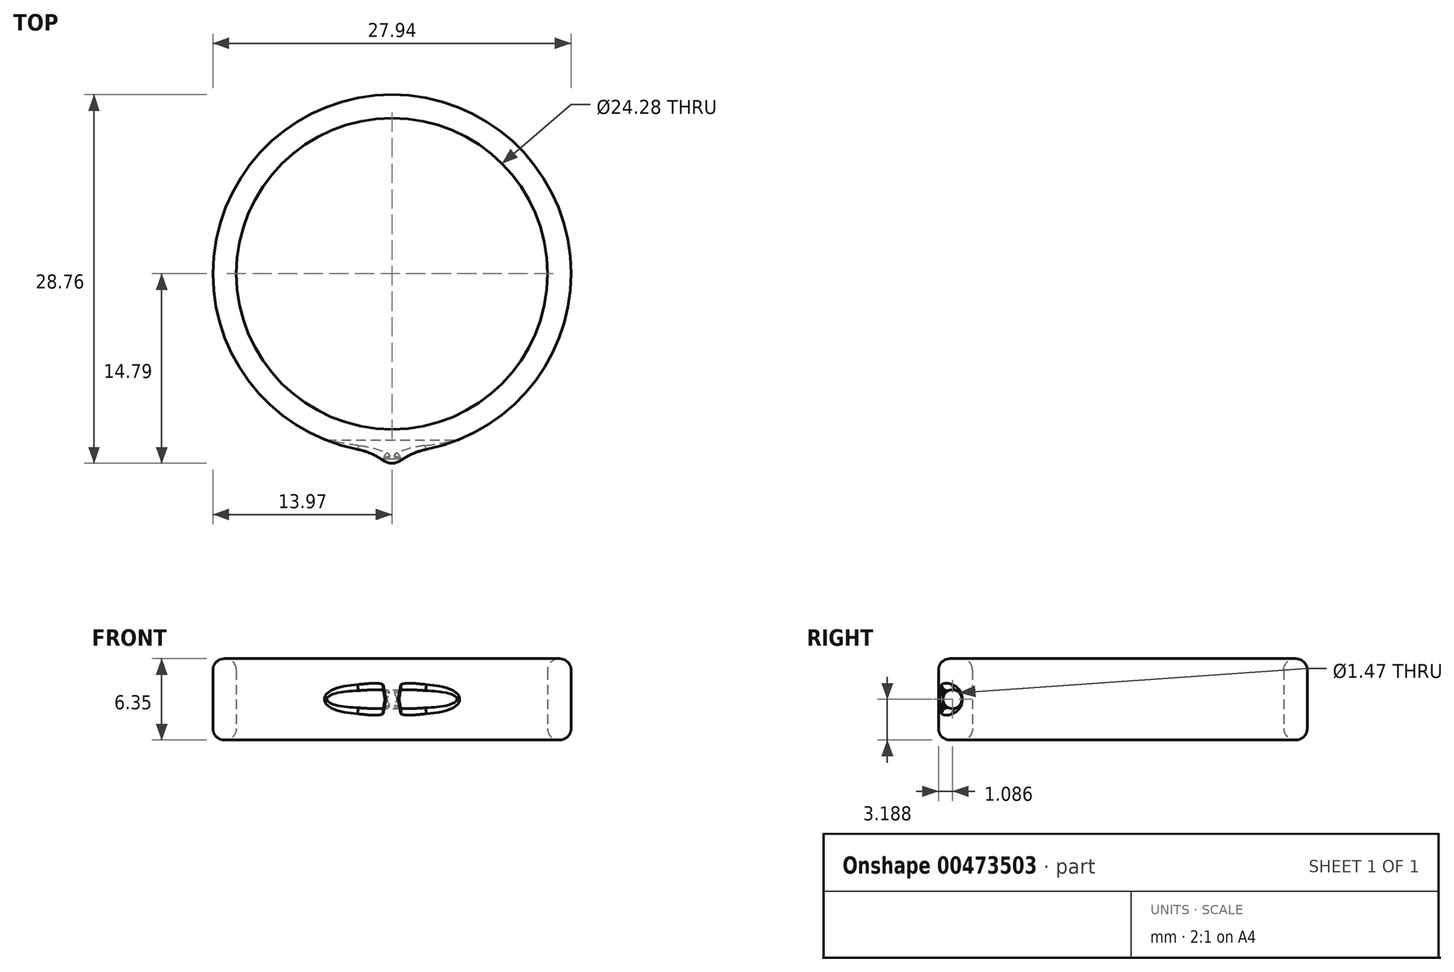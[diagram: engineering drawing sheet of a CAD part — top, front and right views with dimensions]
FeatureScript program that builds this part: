
annotation { "Feature Type Name" : "Feature", "Feature Type Description" : "" }
export const myFeature = defineFeature(function(context is Context, id is Id, definition is map)
    precondition{}
    {
        {
            var Q0;
            Q0=qCreatedBy(makeId("Top.planeOp"),FACE);
            var sketch = newSketch(context, id + "F0", { "sketchPlane" : qUnion([Q0])});
            skCircle(sketch, "E0", {"center": v(0, 0) * mm, "radius": 13.97 * mm});
            skCircle(sketch, "E1", {"center": v(0, 0) * mm, "radius": 12.14 * mm});
            skSolve(sketch);
        }
        {
            var Q0;
            Q0=makeQuery(id+"F0.imprint","IMPRINT",FACE,{"disambiguationData":[TD([[makeQuery(id+"F0.imprint","IMPRINT",EDGE,{"derivedFrom":sQuery(id+"F0.wireOp",EDGE,"E0")}),1.0]])]});
            extrude(context, id + "F1", {"entities" : qUnion([Q0]), "depth" : 6.35 * mm});
        }
        {
            var Q0;
            Q0=qCreatedBy(makeId("Top.planeOp"),FACE);
            var sketch = newSketch(context, id + "F2", { "sketchPlane" : qUnion([Q0])});
            skCircle(sketch, "E2", {"center": v(0, -13.6) * mm, "radius": 1.2 * mm});
            skSolve(sketch);
        }
        {
            var Q0;
            Q0=makeQuery(id+"F2.imprint","IMPRINT",FACE,{"disambiguationData":[TD([[makeQuery(id+"F2.imprint","IMPRINT",EDGE,{"derivedFrom":sQuery(id+"F2.wireOp",EDGE,"E2")}),1.0]])]});
            extrude(context, id + "F3", {"entities" : qUnion([Q0]), "operationType" : NewBodyOperationType.ADD, "depth" : 6.35 * mm});
        }
        {
            var Q0;
            Q0=makeQuery(id+"F3.boolean.opBoolean","INTERSECT",EDGE,{"disambiguationData":[OD(1.0)],"derivedFrom":[makeQuery(id+"F1.opExtrude","SWEPT_FACE",FACE,{"disambiguationData":[OSD([sQuery(id+"F0.wireOp",EDGE,"E0")])]}),makeQuery(id+"F3.opExtrude","SWEPT_FACE",FACE,{"disambiguationData":[OSD([sQuery(id+"F2.wireOp",EDGE,"E2")])]})]});
            var Q1;
            Q1=makeQuery(id+"F3.boolean.opBoolean","INTERSECT",EDGE,{"disambiguationData":[OD(0.0)],"derivedFrom":[makeQuery(id+"F1.opExtrude","SWEPT_FACE",FACE,{"disambiguationData":[OSD([sQuery(id+"F0.wireOp",EDGE,"E0")])]}),makeQuery(id+"F3.opExtrude","SWEPT_FACE",FACE,{"disambiguationData":[OSD([sQuery(id+"F2.wireOp",EDGE,"E2")])]})]});
            fillet(context, id + "F4", {"entities" : qUnion([Q0, Q1]), "radius" : 5.08 * mm, "tangentPropagation" : true, "allowEdgeOverflow" : false});
        }
        {
            var Q0;
            Q0=qCreatedBy(makeId("Right.planeOp"),FACE);
            var sketch = newSketch(context, id + "F5", { "sketchPlane" : qUnion([Q0])});
            skLineSegment(sketch, "E3", {"start": v(-13.7, 0) * mm, "end": v(-13.7, 6.38) * mm});
            skLineSegment(sketch, "E4", {"start": v(-13.7, 6.38) * mm, "end": v(-13.7, 3.19) * mm});
            skCircle(sketch, "E5", {"center": v(-13.7, 3.19) * mm, "radius": 0.73 * mm});
            skSolve(sketch);
        }
        {
            var Q0;
            Q0 = qSketchRegion(id + "F5", true);
            extrude(context, id + "F6", {"entities" : qUnion([Q0]), "operationType" : NewBodyOperationType.REMOVE, "oppositeDirection" : true, "depth" : 25.4 * mm, "hasSecondDirection" : true, "secondDirectionOppositeDirection" : false, "secondDirectionDepth" : 25.4 * mm});
        }
        {
            var Q0;
            Q0=makeQuery(id+"F1.opExtrude","CAP_EDGE",EDGE,{"disambiguationData":[OSD([sQuery(id+"F0.wireOp",EDGE,"E1")])],"isStart":false});
            var Q1;
            {var subQ0=sQuery(id+"F2.wireOp",EDGE,"E2");var subQ1=sQuery(id+"F0.wireOp",EDGE,"E0");Q1=makeQuery(id+"F4.opFillet","BLEND_EDGE",EDGE,{"blendedFrom":[makeQuery(id+"F3.boolean.opBoolean","INTERSECT",EDGE,{"disambiguationData":[OD(1.0)],"derivedFrom":[makeQuery(id+"F1.opExtrude","SWEPT_FACE",FACE,{"disambiguationData":[OSD([subQ1])]}),makeQuery(id+"F3.opExtrude","SWEPT_FACE",FACE,{"disambiguationData":[OSD([subQ0])]})]}),makeQuery(id+"F3.boolean.opBoolean","MERGE",FACE,{"derivedFrom":[makeQuery(id+"F1.opExtrude","CAP_FACE",FACE,{"disambiguationData":[OSD([subQ1,sQuery(id+"F0.wireOp",EDGE,"E1")])],"isStart":false}),makeQuery(id+"F3.opExtrude","CAP_FACE",FACE,{"disambiguationData":[OSD([subQ0])],"isStart":false})]})],"blendedInto":[makeQuery(id+"F3.boolean.opBoolean","MERGE",FACE,{"derivedFrom":[makeQuery(id+"F1.opExtrude","CAP_FACE",FACE,{"disambiguationData":[OSD([subQ1,sQuery(id+"F0.wireOp",EDGE,"E1")])],"isStart":false}),makeQuery(id+"F3.opExtrude","CAP_FACE",FACE,{"disambiguationData":[OSD([subQ0])],"isStart":false})]})]});}
            var Q2;
            Q2=makeQuery(id+"F3.opExtrude","CAP_EDGE",EDGE,{"disambiguationData":[OSD([sQuery(id+"F2.wireOp",EDGE,"E2")])],"isStart":false});
            var Q3;
            {var subQ0=sQuery(id+"F2.wireOp",EDGE,"E2");var subQ1=sQuery(id+"F0.wireOp",EDGE,"E0");Q3=makeQuery(id+"F4.opFillet","BLEND_EDGE",EDGE,{"blendedFrom":[makeQuery(id+"F3.boolean.opBoolean","INTERSECT",EDGE,{"disambiguationData":[OD(0.0)],"derivedFrom":[makeQuery(id+"F1.opExtrude","SWEPT_FACE",FACE,{"disambiguationData":[OSD([subQ1])]}),makeQuery(id+"F3.opExtrude","SWEPT_FACE",FACE,{"disambiguationData":[OSD([subQ0])]})]}),makeQuery(id+"F3.boolean.opBoolean","MERGE",FACE,{"derivedFrom":[makeQuery(id+"F1.opExtrude","CAP_FACE",FACE,{"disambiguationData":[OSD([subQ1,sQuery(id+"F0.wireOp",EDGE,"E1")])],"isStart":false}),makeQuery(id+"F3.opExtrude","CAP_FACE",FACE,{"disambiguationData":[OSD([subQ0])],"isStart":false})]})],"blendedInto":[makeQuery(id+"F3.boolean.opBoolean","MERGE",FACE,{"derivedFrom":[makeQuery(id+"F1.opExtrude","CAP_FACE",FACE,{"disambiguationData":[OSD([subQ1,sQuery(id+"F0.wireOp",EDGE,"E1")])],"isStart":false}),makeQuery(id+"F3.opExtrude","CAP_FACE",FACE,{"disambiguationData":[OSD([subQ0])],"isStart":false})]})]});}
            var Q4;
            Q4=makeQuery(id+"F1.opExtrude","CAP_EDGE",EDGE,{"disambiguationData":[OSD([sQuery(id+"F0.wireOp",EDGE,"E0")])],"isStart":false});
            var Q5;
            {var subQ0=sQuery(id+"F2.wireOp",EDGE,"E2");var subQ1=sQuery(id+"F0.wireOp",EDGE,"E0");Q5=makeQuery(id+"F4.opFillet","BLEND_EDGE",EDGE,{"blendedFrom":[makeQuery(id+"F3.boolean.opBoolean","INTERSECT",EDGE,{"disambiguationData":[OD(0.0)],"derivedFrom":[makeQuery(id+"F1.opExtrude","SWEPT_FACE",FACE,{"disambiguationData":[OSD([subQ1])]}),makeQuery(id+"F3.opExtrude","SWEPT_FACE",FACE,{"disambiguationData":[OSD([subQ0])]})]}),makeQuery(id+"F3.boolean.opBoolean","MERGE",FACE,{"derivedFrom":[makeQuery(id+"F1.opExtrude","CAP_FACE",FACE,{"disambiguationData":[OSD([subQ1,sQuery(id+"F0.wireOp",EDGE,"E1")])],"isStart":true}),makeQuery(id+"F3.opExtrude","CAP_FACE",FACE,{"disambiguationData":[OSD([subQ0])],"isStart":true})]})],"blendedInto":[makeQuery(id+"F3.boolean.opBoolean","MERGE",FACE,{"derivedFrom":[makeQuery(id+"F1.opExtrude","CAP_FACE",FACE,{"disambiguationData":[OSD([subQ1,sQuery(id+"F0.wireOp",EDGE,"E1")])],"isStart":true}),makeQuery(id+"F3.opExtrude","CAP_FACE",FACE,{"disambiguationData":[OSD([subQ0])],"isStart":true})]})]});}
            var Q6;
            Q6=makeQuery(id+"F1.opExtrude","CAP_EDGE",EDGE,{"disambiguationData":[OSD([sQuery(id+"F0.wireOp",EDGE,"E0")])],"isStart":true});
            var Q7;
            Q7=makeQuery(id+"F3.opExtrude","CAP_EDGE",EDGE,{"disambiguationData":[OSD([sQuery(id+"F2.wireOp",EDGE,"E2")])],"isStart":true});
            var Q8;
            {var subQ0=sQuery(id+"F2.wireOp",EDGE,"E2");var subQ1=sQuery(id+"F0.wireOp",EDGE,"E0");Q8=makeQuery(id+"F4.opFillet","BLEND_EDGE",EDGE,{"blendedFrom":[makeQuery(id+"F3.boolean.opBoolean","INTERSECT",EDGE,{"disambiguationData":[OD(1.0)],"derivedFrom":[makeQuery(id+"F1.opExtrude","SWEPT_FACE",FACE,{"disambiguationData":[OSD([subQ1])]}),makeQuery(id+"F3.opExtrude","SWEPT_FACE",FACE,{"disambiguationData":[OSD([subQ0])]})]}),makeQuery(id+"F3.boolean.opBoolean","MERGE",FACE,{"derivedFrom":[makeQuery(id+"F1.opExtrude","CAP_FACE",FACE,{"disambiguationData":[OSD([subQ1,sQuery(id+"F0.wireOp",EDGE,"E1")])],"isStart":true}),makeQuery(id+"F3.opExtrude","CAP_FACE",FACE,{"disambiguationData":[OSD([subQ0])],"isStart":true})]})],"blendedInto":[makeQuery(id+"F3.boolean.opBoolean","MERGE",FACE,{"derivedFrom":[makeQuery(id+"F1.opExtrude","CAP_FACE",FACE,{"disambiguationData":[OSD([subQ1,sQuery(id+"F0.wireOp",EDGE,"E1")])],"isStart":true}),makeQuery(id+"F3.opExtrude","CAP_FACE",FACE,{"disambiguationData":[OSD([subQ0])],"isStart":true})]})]});}
            var Q9;
            Q9=makeQuery(id+"F1.opExtrude","CAP_EDGE",EDGE,{"disambiguationData":[OSD([sQuery(id+"F0.wireOp",EDGE,"E1")])],"isStart":true});
            fillet(context, id + "F7", {"entities" : qUnion([Q0, Q1, Q2, Q3, Q4, Q5, Q6, Q7, Q8, Q9]), "radius" : 0.89 * mm, "tangentPropagation" : true, "allowEdgeOverflow" : false});
        }
        {
            var Q0;
            {var subQ0=sQuery(id+"F2.wireOp",EDGE,"E2");var subQ1=sQuery(id+"F0.wireOp",EDGE,"E0");Q0=makeQuery(id+"F6.boolean.opBoolean","INTERSECT",EDGE,{"derivedFrom":[makeQuery(id+"F4.opFillet","BLEND_FACE",FACE,{"disambiguationData":[OSD([subQ1,subQ0]),TDD([makeQuery(id+"F3.boolean.opBoolean","INTERSECT",EDGE,{"disambiguationData":[OD(0.0)],"derivedFrom":[makeQuery(id+"F1.opExtrude","SWEPT_FACE",FACE,{"disambiguationData":[OSD([subQ1])]}),makeQuery(id+"F3.opExtrude","SWEPT_FACE",FACE,{"disambiguationData":[OSD([subQ0])]})]})])]}),makeQuery(id+"F6.opExtrude","SWEPT_FACE",FACE,{"disambiguationData":[OSD([sQuery(id+"F5.wireOp",EDGE,"E5")])]})]});}
            var Q1;
            {var subQ0=sQuery(id+"F2.wireOp",EDGE,"E2");var subQ1=sQuery(id+"F0.wireOp",EDGE,"E0");Q1=makeQuery(id+"F6.boolean.opBoolean","INTERSECT",EDGE,{"derivedFrom":[makeQuery(id+"F4.opFillet","BLEND_FACE",FACE,{"disambiguationData":[OSD([subQ1,subQ0]),TDD([makeQuery(id+"F3.boolean.opBoolean","INTERSECT",EDGE,{"disambiguationData":[OD(1.0)],"derivedFrom":[makeQuery(id+"F1.opExtrude","SWEPT_FACE",FACE,{"disambiguationData":[OSD([subQ1])]}),makeQuery(id+"F3.opExtrude","SWEPT_FACE",FACE,{"disambiguationData":[OSD([subQ0])]})]})])]}),makeQuery(id+"F6.opExtrude","SWEPT_FACE",FACE,{"disambiguationData":[OSD([sQuery(id+"F5.wireOp",EDGE,"E5")])]})]});}
            fillet(context, id + "F8", {"entities" : qUnion([Q0, Q1]), "radius" : 0.5 * mm, "tangentPropagation" : true, "allowEdgeOverflow" : false});
        }
        {
            var Q0;
            {var subQ0=sQuery(id+"F2.wireOp",EDGE,"E2");var subQ1=makeQuery(id+"F3.opExtrude","SWEPT_FACE",FACE,{"disambiguationData":[OSD([subQ0])]});var subQ2=sQuery(id+"F0.wireOp",EDGE,"E0");Q0=makeQuery(id+"F8.opFillet","BLEND_EDGE",EDGE,{"disambiguationData":[OD(2.0)],"blendedFrom":[makeQuery(id+"F6.boolean.opBoolean","INTERSECT",EDGE,{"derivedFrom":[makeQuery(id+"F4.opFillet","BLEND_FACE",FACE,{"disambiguationData":[OSD([subQ2,subQ0]),TDD([makeQuery(id+"F3.boolean.opBoolean","INTERSECT",EDGE,{"disambiguationData":[OD(0.0)],"derivedFrom":[makeQuery(id+"F1.opExtrude","SWEPT_FACE",FACE,{"disambiguationData":[OSD([subQ2])]}),subQ1]})])]}),makeQuery(id+"F6.opExtrude","SWEPT_FACE",FACE,{"disambiguationData":[OSD([sQuery(id+"F5.wireOp",EDGE,"E5")])]})]}),subQ1],"blendedInto":[subQ1]});}
            var Q1;
            {var subQ0=sQuery(id+"F2.wireOp",EDGE,"E2");var subQ1=makeQuery(id+"F3.opExtrude","SWEPT_FACE",FACE,{"disambiguationData":[OSD([subQ0])]});var subQ2=sQuery(id+"F0.wireOp",EDGE,"E0");Q1=makeQuery(id+"F8.opFillet","BLEND_EDGE",EDGE,{"disambiguationData":[OD(1.0)],"blendedFrom":[makeQuery(id+"F6.boolean.opBoolean","INTERSECT",EDGE,{"derivedFrom":[makeQuery(id+"F4.opFillet","BLEND_FACE",FACE,{"disambiguationData":[OSD([subQ2,subQ0]),TDD([makeQuery(id+"F3.boolean.opBoolean","INTERSECT",EDGE,{"disambiguationData":[OD(1.0)],"derivedFrom":[makeQuery(id+"F1.opExtrude","SWEPT_FACE",FACE,{"disambiguationData":[OSD([subQ2])]}),subQ1]})])]}),makeQuery(id+"F6.opExtrude","SWEPT_FACE",FACE,{"disambiguationData":[OSD([sQuery(id+"F5.wireOp",EDGE,"E5")])]})]}),subQ1],"blendedInto":[subQ1]});}
            var Q2;
            {var subQ0=sQuery(id+"F2.wireOp",EDGE,"E2");var subQ1=makeQuery(id+"F3.opExtrude","SWEPT_FACE",FACE,{"disambiguationData":[OSD([subQ0])]});var subQ2=sQuery(id+"F0.wireOp",EDGE,"E0");Q2=makeQuery(id+"F8.opFillet","BLEND_EDGE",EDGE,{"disambiguationData":[OD(0.0)],"blendedFrom":[makeQuery(id+"F6.boolean.opBoolean","INTERSECT",EDGE,{"derivedFrom":[makeQuery(id+"F4.opFillet","BLEND_FACE",FACE,{"disambiguationData":[OSD([subQ2,subQ0]),TDD([makeQuery(id+"F3.boolean.opBoolean","INTERSECT",EDGE,{"disambiguationData":[OD(1.0)],"derivedFrom":[makeQuery(id+"F1.opExtrude","SWEPT_FACE",FACE,{"disambiguationData":[OSD([subQ2])]}),subQ1]})])]}),makeQuery(id+"F6.opExtrude","SWEPT_FACE",FACE,{"disambiguationData":[OSD([sQuery(id+"F5.wireOp",EDGE,"E5")])]})]}),subQ1],"blendedInto":[subQ1]});}
            var Q3;
            {var subQ0=sQuery(id+"F2.wireOp",EDGE,"E2");var subQ1=makeQuery(id+"F3.opExtrude","SWEPT_FACE",FACE,{"disambiguationData":[OSD([subQ0])]});var subQ2=sQuery(id+"F0.wireOp",EDGE,"E0");Q3=makeQuery(id+"F8.opFillet","BLEND_EDGE",EDGE,{"disambiguationData":[OD(0.0)],"blendedFrom":[makeQuery(id+"F6.boolean.opBoolean","INTERSECT",EDGE,{"derivedFrom":[makeQuery(id+"F4.opFillet","BLEND_FACE",FACE,{"disambiguationData":[OSD([subQ2,subQ0]),TDD([makeQuery(id+"F3.boolean.opBoolean","INTERSECT",EDGE,{"disambiguationData":[OD(0.0)],"derivedFrom":[makeQuery(id+"F1.opExtrude","SWEPT_FACE",FACE,{"disambiguationData":[OSD([subQ2])]}),subQ1]})])]}),makeQuery(id+"F6.opExtrude","SWEPT_FACE",FACE,{"disambiguationData":[OSD([sQuery(id+"F5.wireOp",EDGE,"E5")])]})]}),subQ1],"blendedInto":[subQ1]});}
            var Q4;
            {var subQ0=sQuery(id+"F2.wireOp",EDGE,"E2");var subQ1=makeQuery(id+"F3.opExtrude","SWEPT_FACE",FACE,{"disambiguationData":[OSD([subQ0])]});var subQ2=sQuery(id+"F0.wireOp",EDGE,"E0");Q4=makeQuery(id+"F8.opFillet","BLEND_EDGE",EDGE,{"disambiguationData":[OD(1.0)],"blendedFrom":[makeQuery(id+"F6.boolean.opBoolean","INTERSECT",EDGE,{"derivedFrom":[makeQuery(id+"F4.opFillet","BLEND_FACE",FACE,{"disambiguationData":[OSD([subQ2,subQ0]),TDD([makeQuery(id+"F3.boolean.opBoolean","INTERSECT",EDGE,{"disambiguationData":[OD(0.0)],"derivedFrom":[makeQuery(id+"F1.opExtrude","SWEPT_FACE",FACE,{"disambiguationData":[OSD([subQ2])]}),subQ1]})])]}),makeQuery(id+"F6.opExtrude","SWEPT_FACE",FACE,{"disambiguationData":[OSD([sQuery(id+"F5.wireOp",EDGE,"E5")])]})]}),subQ1],"blendedInto":[subQ1]});}
            var Q5;
            {var subQ0=sQuery(id+"F2.wireOp",EDGE,"E2");var subQ1=makeQuery(id+"F3.opExtrude","SWEPT_FACE",FACE,{"disambiguationData":[OSD([subQ0])]});var subQ2=sQuery(id+"F0.wireOp",EDGE,"E0");Q5=makeQuery(id+"F8.opFillet","BLEND_EDGE",EDGE,{"disambiguationData":[OD(2.0)],"blendedFrom":[makeQuery(id+"F6.boolean.opBoolean","INTERSECT",EDGE,{"derivedFrom":[makeQuery(id+"F4.opFillet","BLEND_FACE",FACE,{"disambiguationData":[OSD([subQ2,subQ0]),TDD([makeQuery(id+"F3.boolean.opBoolean","INTERSECT",EDGE,{"disambiguationData":[OD(1.0)],"derivedFrom":[makeQuery(id+"F1.opExtrude","SWEPT_FACE",FACE,{"disambiguationData":[OSD([subQ2])]}),subQ1]})])]}),makeQuery(id+"F6.opExtrude","SWEPT_FACE",FACE,{"disambiguationData":[OSD([sQuery(id+"F5.wireOp",EDGE,"E5")])]})]}),subQ1],"blendedInto":[subQ1]});}
            fillet(context, id + "F9", {"entities" : qUnion([Q0, Q1, Q2, Q3, Q4, Q5]), "radius" : 0.13 * mm, "tangentPropagation" : true, "allowEdgeOverflow" : false});
        }
    });
